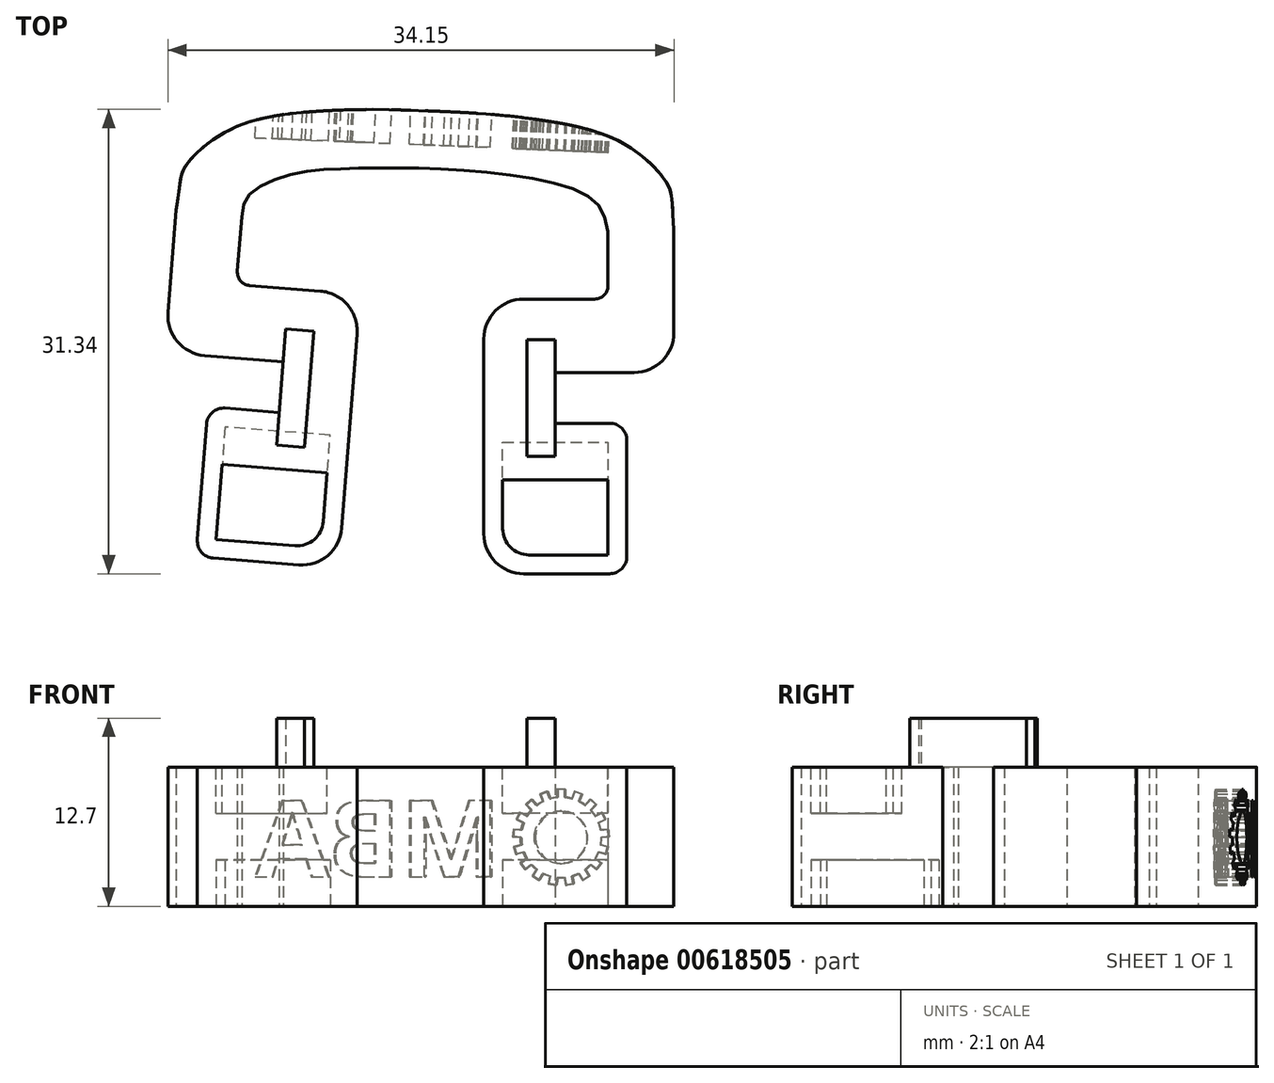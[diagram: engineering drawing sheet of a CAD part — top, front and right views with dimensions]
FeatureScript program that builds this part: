
annotation { "Feature Type Name" : "Feature", "Feature Type Description" : "" }
export const myFeature = defineFeature(function(context is Context, id is Id, definition is map)
    precondition{}
    {
        {
            var Q0;
            Q0=qCreatedBy(makeId("Top.planeOp"),FACE);
            var sketch = newSketch(context, id + "F0", { "sketchPlane" : qUnion([Q0])});
            skLineSegment(sketch, "E0", {"start": v(2.7, -18.54) * mm, "end": v(8.48, -18.54) * mm});
            skLineSegment(sketch, "E1", {"start": v(9.65, -17.37) * mm, "end": v(9.65, -9.55) * mm});
            skLineSegment(sketch, "E2", {"start": v(8.48, -8.38) * mm, "end": v(4.83, -8.38) * mm});
            skLineSegment(sketch, "E3", {"start": v(4.83, -8.38) * mm, "end": v(4.83, -4.95) * mm});
            skLineSegment(sketch, "E4", {"start": v(4.83, -4.95) * mm, "end": v(10.13, -4.95) * mm});
            skLineSegment(sketch, "E5", {"start": v(12.83, -2.26) * mm, "end": v(12.83, 4.7) * mm});
            skLineSegment(sketch, "E6", {"start": v(0, -15.85) * mm, "end": v(0, -2.7) * mm});
            skPoint(sketch, "E7.visualSharp", {"position": v(12.83, -4.95) * mm});
            skArc(sketch, "E7.filletArc", {"start": v(10.13, -4.95) * mm, "mid": v(12.04, -4.16) * mm, "end": v(12.83, -2.26) * mm});
            skPoint(sketch, "E8.visualSharp", {"position": v(9.65, -18.54) * mm});
            skArc(sketch, "E8.filletArc", {"start": v(8.48, -18.54) * mm, "mid": v(9.31, -18.2) * mm, "end": v(9.65, -17.37) * mm});
            skPoint(sketch, "E9.visualSharp", {"position": v(9.65, -8.38) * mm});
            skArc(sketch, "E9.filletArc", {"start": v(9.65, -9.55) * mm, "mid": v(9.31, -8.72) * mm, "end": v(8.48, -8.38) * mm});
            skPoint(sketch, "E10.visualSharp", {"position": v(0, -18.54) * mm});
            skArc(sketch, "E10.filletArc", {"start": v(0, -15.85) * mm, "mid": v(0.79, -17.75) * mm, "end": v(2.7, -18.54) * mm});
            skLineSegment(sketch, "E11", {"start": v(2.7, 0) * mm, "end": v(7.48, 0) * mm});
            skLineSegment(sketch, "E12", {"start": v(8.38, 0.9) * mm, "end": v(8.38, 4.57) * mm});
            skPoint(sketch, "E13.visualSharp", {"position": v(0, 0) * mm});
            skArc(sketch, "E13.filletArc", {"start": v(2.7, 0) * mm, "mid": v(0.79, -0.79) * mm, "end": v(0, -2.7) * mm});
            skPoint(sketch, "E14.visualSharp", {"position": v(8.38, 0) * mm});
            skArc(sketch, "E14.filletArc", {"start": v(7.48, 0) * mm, "mid": v(8.12, 0.26) * mm, "end": v(8.38, 0.9) * mm});
            skFitSpline(sketch, "E15", {"points": [v(12.83, 4.7) * mm, v(12.43, 7.7) * mm, v(9.35, 10.54) * mm, v(3.79, 12.1) * mm, v(-3.68, 12.7) * mm], "startDerivative": vector(-2.52, 27.94) * mm, "endDerivative": vector(-36.03, 1.35) * mm});
            skPoint(sketch, "E16.endSnap0", {"position": v(5.59, -18.54) * mm});
            skArc(sketch, "E17.MirrorCS", {"start": v(-18.72, -8.43) * mm, "mid": v(-18.32, -7.64) * mm, "end": v(-17.47, -7.36) * mm});
            skArc(sketch, "E18.MirrorCS", {"start": v(-18.26, -17.5) * mm, "mid": v(-19.06, -17.09) * mm, "end": v(-19.34, -16.24) * mm});
            skArc(sketch, "E19.MirrorCS", {"start": v(-15.81, 0.92) * mm, "mid": v(-16.42, 1.23) * mm, "end": v(-16.64, 1.88) * mm});
            skArc(sketch, "E20.MirrorCS", {"start": v(-18.84, -3.81) * mm, "mid": v(-20.68, -2.88) * mm, "end": v(-21.32, -0.92) * mm});
            skArc(sketch, "E21.MirrorCS", {"start": v(-9.6, -15.47) * mm, "mid": v(-10.53, -17.3) * mm, "end": v(-12.5, -17.95) * mm});
            skArc(sketch, "E22.MirrorCS", {"start": v(-11.04, 0.54) * mm, "mid": v(-9.2, -0.4) * mm, "end": v(-8.56, -2.36) * mm});
            skLineSegment(sketch, "E23.MirrorCS", {"start": v(-17.47, -7.36) * mm, "end": v(-13.82, -7.65) * mm});
            skLineSegment(sketch, "E24.MirrorCS", {"start": v(-13.82, -7.65) * mm, "end": v(-13.55, -4.23) * mm});
            skLineSegment(sketch, "E25.MirrorCS", {"start": v(-11.04, 0.54) * mm, "end": v(-15.81, 0.92) * mm});
            skLineSegment(sketch, "E26.MirrorCS", {"start": v(-13.55, -4.23) * mm, "end": v(-18.84, -3.81) * mm});
            skLineSegment(sketch, "E27.MirrorCS", {"start": v(-16.64, 1.88) * mm, "end": v(-16.35, 5.54) * mm});
            skLineSegment(sketch, "E28.MirrorCS", {"start": v(-12.5, -17.95) * mm, "end": v(-18.26, -17.5) * mm});
            skFitSpline(sketch, "E29.MirrorCS", {"points": [v(-20.77, 6.02) * mm, v(-20.13, 8.98) * mm, v(-16.85, 11.57) * mm, v(-11.18, 12.68) * mm, v(-3.68, 12.7) * mm], "startDerivative": vector(4.7, 27.65) * mm, "endDerivative": vector(36.02, -1.48) * mm});
            skLineSegment(sketch, "E30.MirrorCS", {"start": v(-9.6, -15.47) * mm, "end": v(-8.56, -2.36) * mm});
            skPoint(sketch, "E31.MirrorP", {"position": v(-21.53, -3.6) * mm});
            skPoint(sketch, "E32.MirrorP", {"position": v(-8.35, 0.33) * mm});
            skPoint(sketch, "E33.MirrorP", {"position": v(-16.7, 0.99) * mm});
            skLineSegment(sketch, "E34.MirrorCS", {"start": v(-19.34, -16.24) * mm, "end": v(-18.72, -8.43) * mm});
            skLineSegment(sketch, "E35.MirrorCS", {"start": v(-21.32, -0.92) * mm, "end": v(-20.77, 6.02) * mm});
            skPoint(sketch, "E36.MirrorP", {"position": v(-19.43, -17.4) * mm});
            skPoint(sketch, "E37.MirrorP", {"position": v(-9.8, -18.16) * mm});
            skPoint(sketch, "E38.MirrorP", {"position": v(-18.63, -7.27) * mm});
            skPoint(sketch, "E39.MirrorP", {"position": v(-15.38, -17.72) * mm});
            skFitSpline(sketch, "E40", {"points": [v(-16.35, 5.54) * mm, v(-15.64, 7.24) * mm, v(-12.74, 8.47) * mm, v(-9.06, 8.82) * mm, v(-3.88, 8.82) * mm, v(2.92, 8.2) * mm, v(7.36, 6.71) * mm, v(8.38, 4.57) * mm], "startDerivative": vector(0.51, 21.81) * mm, "endDerivative": vector(4.3, -24.8) * mm});
            skSolve(sketch);
        }
        {
            var Q0;
            Q0=makeQuery(id+"F0.imprint","IMPRINT",FACE,{"disambiguationData":[TD([[makeQuery(id+"F0.imprint","IMPRINT",EDGE,{"derivedFrom":sQuery(id+"F0.wireOp",EDGE,"E0")}),1.0]])]});
            extrude(context, id + "F1", {"entities" : qUnion([Q0]), "depth" : 9.4 * mm, "offsetDistance" : 25.4 * mm});
        }
        {
            var Q0;
            Q0=makeQuery(id+"F1.opExtrude","CAP_FACE",FACE,{"disambiguationData":[OSD([sQuery(id+"F0.wireOp",EDGE,"E0"),sQuery(id+"F0.wireOp",EDGE,"E1"),sQuery(id+"F0.wireOp",EDGE,"E2"),sQuery(id+"F0.wireOp",EDGE,"E3"),sQuery(id+"F0.wireOp",EDGE,"E4"),sQuery(id+"F0.wireOp",EDGE,"E5"),sQuery(id+"F0.wireOp",EDGE,"E6"),sQuery(id+"F0.wireOp",EDGE,"E7.filletArc"),sQuery(id+"F0.wireOp",EDGE,"E8.filletArc"),sQuery(id+"F0.wireOp",EDGE,"E9.filletArc"),sQuery(id+"F0.wireOp",EDGE,"E10.filletArc"),sQuery(id+"F0.wireOp",EDGE,"E11"),sQuery(id+"F0.wireOp",EDGE,"E12"),sQuery(id+"F0.wireOp",EDGE,"E13.filletArc"),sQuery(id+"F0.wireOp",EDGE,"E14.filletArc"),sQuery(id+"F0.wireOp",EDGE,"E15"),sQuery(id+"F0.wireOp",EDGE,"E17.MirrorCS"),sQuery(id+"F0.wireOp",EDGE,"E18.MirrorCS"),sQuery(id+"F0.wireOp",EDGE,"E19.MirrorCS"),sQuery(id+"F0.wireOp",EDGE,"E20.MirrorCS"),sQuery(id+"F0.wireOp",EDGE,"E21.MirrorCS"),sQuery(id+"F0.wireOp",EDGE,"E22.MirrorCS"),sQuery(id+"F0.wireOp",EDGE,"E23.MirrorCS"),sQuery(id+"F0.wireOp",EDGE,"E24.MirrorCS"),sQuery(id+"F0.wireOp",EDGE,"E25.MirrorCS"),sQuery(id+"F0.wireOp",EDGE,"E26.MirrorCS"),sQuery(id+"F0.wireOp",EDGE,"E27.MirrorCS"),sQuery(id+"F0.wireOp",EDGE,"E28.MirrorCS"),sQuery(id+"F0.wireOp",EDGE,"E29.MirrorCS"),sQuery(id+"F0.wireOp",EDGE,"E30.MirrorCS"),sQuery(id+"F0.wireOp",EDGE,"E34.MirrorCS"),sQuery(id+"F0.wireOp",EDGE,"E35.MirrorCS"),sQuery(id+"F0.wireOp",EDGE,"E40")])],"isStart":false});
            var sketch = newSketch(context, id + "F2", { "sketchPlane" : qUnion([Q0])});
            skPoint(sketch, "E41.endSnap0", {"position": v(-10.53, -17.3) * mm});
            skLineSegment(sketch, "E42", {"start": v(-10.72, -13.57) * mm, "end": v(-10.83, -15.02) * mm});
            skLineSegment(sketch, "E43", {"start": v(-18.06, -16.23) * mm, "end": v(-17.66, -11.17) * mm});
            skLineSegment(sketch, "E44", {"start": v(-18.06, -16.23) * mm, "end": v(-12.74, -16.65) * mm});
            skPoint(sketch, "E45.visualSharp", {"position": v(-10.97, -16.8) * mm});
            skArc(sketch, "E45.filletArc", {"start": v(-12.74, -16.65) * mm, "mid": v(-11.45, -16.23) * mm, "end": v(-10.83, -15.02) * mm});
            skLineSegment(sketch, "E46", {"start": v(-17.66, -11.17) * mm, "end": v(-10.57, -11.73) * mm});
            skLineSegment(sketch, "E47", {"start": v(-10.72, -13.57) * mm, "end": v(-10.57, -11.73) * mm});
            skPoint(sketch, "E48", {"position": v(-10.57, -11.73) * mm});
            skLineSegment(sketch, "E49.MirrorCS", {"start": v(1.27, -14.04) * mm, "end": v(1.27, -12.2) * mm});
            skPoint(sketch, "E50.MirrorP", {"position": v(1.27, -12.2) * mm});
            skPoint(sketch, "E51.MirrorP", {"position": v(0.79, -17.75) * mm});
            skLineSegment(sketch, "E52.MirrorCS", {"start": v(8.38, -17.27) * mm, "end": v(3.05, -17.27) * mm});
            skLineSegment(sketch, "E53.MirrorCS", {"start": v(8.38, -17.27) * mm, "end": v(8.38, -12.2) * mm});
            skLineSegment(sketch, "E54.MirrorCS", {"start": v(8.38, -12.2) * mm, "end": v(1.27, -12.2) * mm});
            skLineSegment(sketch, "E55.MirrorCS", {"start": v(1.27, -14.04) * mm, "end": v(1.27, -15.5) * mm});
            skArc(sketch, "E56.MirrorCS", {"start": v(3.05, -17.27) * mm, "mid": v(1.8, -16.75) * mm, "end": v(1.27, -15.5) * mm});
            skSolve(sketch);
        }
        {
            var Q0;
            Q0=makeQuery(id+"F2.imprint","IMPRINT",FACE,{"disambiguationData":[TD([[makeQuery(id+"F2.imprint","IMPRINT",EDGE,{"derivedFrom":sQuery(id+"F2.wireOp",EDGE,"E42")}),-1.0]])]});
            var Q1;
            Q1=makeQuery(id+"F2.imprint","IMPRINT",FACE,{"disambiguationData":[TD([[makeQuery(id+"F2.imprint","IMPRINT",EDGE,{"derivedFrom":sQuery(id+"F2.wireOp",EDGE,"E49.MirrorCS")}),-1.0]])]});
            extrude(context, id + "F3", {"entities" : qUnion([Q0, Q1]), "operationType" : NewBodyOperationType.REMOVE, "oppositeDirection" : true, "depth" : 3.12 * mm, "offsetDistance" : 25.4 * mm});
        }
        {
            var Q0;
            Q0=makeQuery(id+"F1.opExtrude","CAP_FACE",FACE,{"disambiguationData":[OSD([sQuery(id+"F0.wireOp",EDGE,"E0"),sQuery(id+"F0.wireOp",EDGE,"E1"),sQuery(id+"F0.wireOp",EDGE,"E2"),sQuery(id+"F0.wireOp",EDGE,"E3"),sQuery(id+"F0.wireOp",EDGE,"E4"),sQuery(id+"F0.wireOp",EDGE,"E5"),sQuery(id+"F0.wireOp",EDGE,"E6"),sQuery(id+"F0.wireOp",EDGE,"E7.filletArc"),sQuery(id+"F0.wireOp",EDGE,"E8.filletArc"),sQuery(id+"F0.wireOp",EDGE,"E9.filletArc"),sQuery(id+"F0.wireOp",EDGE,"E10.filletArc"),sQuery(id+"F0.wireOp",EDGE,"E11"),sQuery(id+"F0.wireOp",EDGE,"E12"),sQuery(id+"F0.wireOp",EDGE,"E13.filletArc"),sQuery(id+"F0.wireOp",EDGE,"E14.filletArc"),sQuery(id+"F0.wireOp",EDGE,"E15"),sQuery(id+"F0.wireOp",EDGE,"E17.MirrorCS"),sQuery(id+"F0.wireOp",EDGE,"E18.MirrorCS"),sQuery(id+"F0.wireOp",EDGE,"E19.MirrorCS"),sQuery(id+"F0.wireOp",EDGE,"E20.MirrorCS"),sQuery(id+"F0.wireOp",EDGE,"E21.MirrorCS"),sQuery(id+"F0.wireOp",EDGE,"E22.MirrorCS"),sQuery(id+"F0.wireOp",EDGE,"E23.MirrorCS"),sQuery(id+"F0.wireOp",EDGE,"E24.MirrorCS"),sQuery(id+"F0.wireOp",EDGE,"E25.MirrorCS"),sQuery(id+"F0.wireOp",EDGE,"E26.MirrorCS"),sQuery(id+"F0.wireOp",EDGE,"E27.MirrorCS"),sQuery(id+"F0.wireOp",EDGE,"E28.MirrorCS"),sQuery(id+"F0.wireOp",EDGE,"E29.MirrorCS"),sQuery(id+"F0.wireOp",EDGE,"E30.MirrorCS"),sQuery(id+"F0.wireOp",EDGE,"E34.MirrorCS"),sQuery(id+"F0.wireOp",EDGE,"E35.MirrorCS"),sQuery(id+"F0.wireOp",EDGE,"E40")])],"isStart":true});
            var sketch = newSketch(context, id + "F4", { "sketchPlane" : qUnion([Q0])});
            skLineSegment(sketch, "E57", {"start": v(8.38, 17.27) * mm, "end": v(3.05, 17.27) * mm});
            skLineSegment(sketch, "E58", {"start": v(1.27, 15.5) * mm, "end": v(1.27, 9.65) * mm});
            skLineSegment(sketch, "E59", {"start": v(1.27, 9.65) * mm, "end": v(8.38, 9.65) * mm});
            skLineSegment(sketch, "E60", {"start": v(8.38, 9.65) * mm, "end": v(8.38, 17.27) * mm});
            skPoint(sketch, "E61.visualSharp", {"position": v(1.27, 17.27) * mm});
            skArc(sketch, "E61.filletArc", {"start": v(3.05, 17.27) * mm, "mid": v(1.8, 16.75) * mm, "end": v(1.27, 15.5) * mm});
            skLineSegment(sketch, "E62.MirrorCS", {"start": v(-18.06, 16.23) * mm, "end": v(-12.74, 16.65) * mm});
            skPoint(sketch, "E63.MirrorP", {"position": v(-10.97, 16.8) * mm});
            skLineSegment(sketch, "E64.MirrorCS", {"start": v(-10.37, 9.2) * mm, "end": v(-17.46, 8.64) * mm});
            skLineSegment(sketch, "E65.MirrorCS", {"start": v(-17.46, 8.64) * mm, "end": v(-18.06, 16.23) * mm});
            skLineSegment(sketch, "E66.MirrorCS", {"start": v(-10.83, 15.02) * mm, "end": v(-10.37, 9.2) * mm});
            skArc(sketch, "E67.MirrorCS", {"start": v(-12.74, 16.65) * mm, "mid": v(-11.45, 16.23) * mm, "end": v(-10.83, 15.02) * mm});
            skSolve(sketch);
        }
        {
            var Q0;
            Q0 = qSketchRegion(id + "F4", true);
            extrude(context, id + "F5", {"entities" : qUnion([Q0]), "operationType" : NewBodyOperationType.REMOVE, "oppositeDirection" : true, "depth" : 3.12 * mm, "offsetDistance" : 25.4 * mm});
        }
        {
            var Q0;
            Q0=makeQuery(id+"F1.opExtrude","CAP_FACE",FACE,{"disambiguationData":[OSD([sQuery(id+"F0.wireOp",EDGE,"E0"),sQuery(id+"F0.wireOp",EDGE,"E1"),sQuery(id+"F0.wireOp",EDGE,"E2"),sQuery(id+"F0.wireOp",EDGE,"E3"),sQuery(id+"F0.wireOp",EDGE,"E4"),sQuery(id+"F0.wireOp",EDGE,"E5"),sQuery(id+"F0.wireOp",EDGE,"E6"),sQuery(id+"F0.wireOp",EDGE,"E7.filletArc"),sQuery(id+"F0.wireOp",EDGE,"E8.filletArc"),sQuery(id+"F0.wireOp",EDGE,"E9.filletArc"),sQuery(id+"F0.wireOp",EDGE,"E10.filletArc"),sQuery(id+"F0.wireOp",EDGE,"E11"),sQuery(id+"F0.wireOp",EDGE,"E12"),sQuery(id+"F0.wireOp",EDGE,"E13.filletArc"),sQuery(id+"F0.wireOp",EDGE,"E14.filletArc"),sQuery(id+"F0.wireOp",EDGE,"E15"),sQuery(id+"F0.wireOp",EDGE,"E17.MirrorCS"),sQuery(id+"F0.wireOp",EDGE,"E18.MirrorCS"),sQuery(id+"F0.wireOp",EDGE,"E19.MirrorCS"),sQuery(id+"F0.wireOp",EDGE,"E20.MirrorCS"),sQuery(id+"F0.wireOp",EDGE,"E21.MirrorCS"),sQuery(id+"F0.wireOp",EDGE,"E22.MirrorCS"),sQuery(id+"F0.wireOp",EDGE,"E23.MirrorCS"),sQuery(id+"F0.wireOp",EDGE,"E24.MirrorCS"),sQuery(id+"F0.wireOp",EDGE,"E25.MirrorCS"),sQuery(id+"F0.wireOp",EDGE,"E26.MirrorCS"),sQuery(id+"F0.wireOp",EDGE,"E27.MirrorCS"),sQuery(id+"F0.wireOp",EDGE,"E28.MirrorCS"),sQuery(id+"F0.wireOp",EDGE,"E29.MirrorCS"),sQuery(id+"F0.wireOp",EDGE,"E30.MirrorCS"),sQuery(id+"F0.wireOp",EDGE,"E34.MirrorCS"),sQuery(id+"F0.wireOp",EDGE,"E35.MirrorCS"),sQuery(id+"F0.wireOp",EDGE,"E40")])],"isStart":false});
            var sketch = newSketch(context, id + "F6", { "sketchPlane" : qUnion([Q0])});
            skLineSegment(sketch, "E68", {"start": v(-13.55, -4.23) * mm, "end": v(-13.38, -2.02) * mm});
            skLineSegment(sketch, "E69", {"start": v(-13.82, -7.65) * mm, "end": v(-14, -9.87) * mm});
            skLineSegment(sketch, "E70", {"start": v(-13.38, -2.02) * mm, "end": v(-11.48, -2.16) * mm});
            skLineSegment(sketch, "E71", {"start": v(-11.48, -2.16) * mm, "end": v(-12.1, -10.01) * mm});
            skLineSegment(sketch, "E72", {"start": v(-12.1, -10.01) * mm, "end": v(-14, -9.87) * mm});
            skLineSegment(sketch, "E73", {"start": v(4.83, -4.95) * mm, "end": v(4.83, -2.73) * mm});
            skLineSegment(sketch, "E74", {"start": v(4.83, -2.73) * mm, "end": v(2.92, -2.73) * mm});
            skLineSegment(sketch, "E75", {"start": v(2.92, -2.73) * mm, "end": v(2.92, -10.6) * mm});
            skLineSegment(sketch, "E76", {"start": v(2.92, -10.6) * mm, "end": v(4.83, -10.6) * mm});
            skLineSegment(sketch, "E77", {"start": v(4.83, -10.6) * mm, "end": v(4.83, -8.38) * mm});
            skSolve(sketch);
        }
        {
            var Q0;
            Q0=makeQuery(id+"F6.imprint","IMPRINT",FACE,{"disambiguationData":[TD([[makeQuery(id+"F6.imprint","IMPRINT",EDGE,{"derivedFrom":sQuery(id+"F6.wireOp",EDGE,"E68")}),-1.0]])]});
            var Q1;
            Q1=makeQuery(id+"F6.imprint","IMPRINT",FACE,{"disambiguationData":[TD([[makeQuery(id+"F6.imprint","IMPRINT",EDGE,{"derivedFrom":sQuery(id+"F6.wireOp",EDGE,"E73")}),1.0]])]});
            extrude(context, id + "F7", {"entities" : qUnion([Q0, Q1]), "operationType" : NewBodyOperationType.ADD, "depth" : 3.3 * mm, "offsetDistance" : 25.4 * mm});
        }
        {
            var Q0;
            Q0=makeQuery(id+"F1.opExtrude","CAP_FACE",FACE,{"disambiguationData":[OSD([sQuery(id+"F0.wireOp",EDGE,"E0"),sQuery(id+"F0.wireOp",EDGE,"E1"),sQuery(id+"F0.wireOp",EDGE,"E2"),sQuery(id+"F0.wireOp",EDGE,"E3"),sQuery(id+"F0.wireOp",EDGE,"E4"),sQuery(id+"F0.wireOp",EDGE,"E5"),sQuery(id+"F0.wireOp",EDGE,"E6"),sQuery(id+"F0.wireOp",EDGE,"E7.filletArc"),sQuery(id+"F0.wireOp",EDGE,"E8.filletArc"),sQuery(id+"F0.wireOp",EDGE,"E9.filletArc"),sQuery(id+"F0.wireOp",EDGE,"E10.filletArc"),sQuery(id+"F0.wireOp",EDGE,"E11"),sQuery(id+"F0.wireOp",EDGE,"E12"),sQuery(id+"F0.wireOp",EDGE,"E13.filletArc"),sQuery(id+"F0.wireOp",EDGE,"E14.filletArc"),sQuery(id+"F0.wireOp",EDGE,"E15"),sQuery(id+"F0.wireOp",EDGE,"E17.MirrorCS"),sQuery(id+"F0.wireOp",EDGE,"E18.MirrorCS"),sQuery(id+"F0.wireOp",EDGE,"E19.MirrorCS"),sQuery(id+"F0.wireOp",EDGE,"E20.MirrorCS"),sQuery(id+"F0.wireOp",EDGE,"E21.MirrorCS"),sQuery(id+"F0.wireOp",EDGE,"E22.MirrorCS"),sQuery(id+"F0.wireOp",EDGE,"E23.MirrorCS"),sQuery(id+"F0.wireOp",EDGE,"E24.MirrorCS"),sQuery(id+"F0.wireOp",EDGE,"E25.MirrorCS"),sQuery(id+"F0.wireOp",EDGE,"E26.MirrorCS"),sQuery(id+"F0.wireOp",EDGE,"E27.MirrorCS"),sQuery(id+"F0.wireOp",EDGE,"E28.MirrorCS"),sQuery(id+"F0.wireOp",EDGE,"E29.MirrorCS"),sQuery(id+"F0.wireOp",EDGE,"E30.MirrorCS"),sQuery(id+"F0.wireOp",EDGE,"E34.MirrorCS"),sQuery(id+"F0.wireOp",EDGE,"E35.MirrorCS"),sQuery(id+"F0.wireOp",EDGE,"E40")])],"isStart":false});
            var sketch = newSketch(context, id + "F8", { "sketchPlane" : qUnion([Q0])});
            skLineSegment(sketch, "E78", {"start": v(-3.68, 12.7) * mm, "end": v(-3.56, 15.72) * mm, "construction": true});
            skLineSegment(sketch, "E79", {"start": v(-5.82, 15.82) * mm, "end": v(-1.3, 15.63) * mm, "construction": true});
            skSolve(sketch);
        }
        {
            var Q0;
            Q0=sQuery(id+"F8.wireOp",EDGE,"E78");
            cPlane(context, id + "F9", {"entities" : qUnion([Q0]), "cplaneType" : CPlaneType.MID_PLANE, "offset" : 25.4 * mm, "width" : 152.4 * mm, "height" : 152.4 * mm});
        }
        {
            var Q0;
            Q0=qCreatedBy(id+"F9.planeOp",FACE);
            var sketch = newSketch(context, id + "F10", { "sketchPlane" : qUnion([Q0])});
            skText(sketch, "E80", { "text": "MBA", "fontName": "OpenSans-Bold.ttf"});
            skArc(sketch, "E81", {"start": v(-5.98, 7.09) * mm, "mid": v(-6.2, 6.97) * mm, "end": v(-6.4, 6.83) * mm});
            skCircle(sketch, "E82", {"center": v(-4.76, 4.65) * mm, "radius": 1.77 * mm});
            skLineSegment(sketch, "E83", {"start": v(-5.02, 7.36) * mm, "end": v(-5.02, 7.88) * mm});
            skLineSegment(sketch, "E84", {"start": v(-5.02, 7.88) * mm, "end": v(-4.5, 7.88) * mm});
            skLineSegment(sketch, "E85", {"start": v(-4.5, 7.88) * mm, "end": v(-4.5, 7.36) * mm});
            skLineSegment(sketch, "E86.1.0", {"start": v(-6.17, 7.57) * mm, "end": v(-5.68, 7.76) * mm});
            skLineSegment(sketch, "E86.1.1", {"start": v(-5.68, 7.76) * mm, "end": v(-5.5, 7.27) * mm});
            skLineSegment(sketch, "E86.1.2", {"start": v(-5.98, 7.09) * mm, "end": v(-6.17, 7.57) * mm});
            skLineSegment(sketch, "E86.2.0", {"start": v(-7.13, 6.86) * mm, "end": v(-6.74, 7.21) * mm});
            skLineSegment(sketch, "E86.2.1", {"start": v(-6.74, 7.21) * mm, "end": v(-6.4, 6.83) * mm});
            skLineSegment(sketch, "E86.2.2", {"start": v(-6.78, 6.48) * mm, "end": v(-7.13, 6.86) * mm});
            skLineSegment(sketch, "E87.1.3.0", {"start": v(-7.77, 5.86) * mm, "end": v(-7.53, 6.32) * mm});
            skLineSegment(sketch, "E87.3.3.0", {"start": v(-7.53, 6.32) * mm, "end": v(-7.07, 6.1) * mm});
            skLineSegment(sketch, "E87.6.3.0", {"start": v(-7.3, 5.63) * mm, "end": v(-7.77, 5.86) * mm});
            skLineSegment(sketch, "E87.1.4.0", {"start": v(-8, 4.7) * mm, "end": v(-7.95, 5.2) * mm});
            skLineSegment(sketch, "E87.3.4.0", {"start": v(-7.95, 5.2) * mm, "end": v(-7.44, 5.16) * mm});
            skLineSegment(sketch, "E87.6.4.0", {"start": v(-7.48, 4.64) * mm, "end": v(-8, 4.7) * mm});
            skLineSegment(sketch, "E87.1.5.0", {"start": v(-7.8, 3.52) * mm, "end": v(-7.94, 4.02) * mm});
            skLineSegment(sketch, "E87.3.5.0", {"start": v(-7.94, 4.02) * mm, "end": v(-7.44, 4.16) * mm});
            skLineSegment(sketch, "E87.6.5.0", {"start": v(-7.3, 3.66) * mm, "end": v(-7.8, 3.52) * mm});
            skLineSegment(sketch, "E87.1.6.0", {"start": v(-7.18, 2.5) * mm, "end": v(-7.5, 2.91) * mm});
            skLineSegment(sketch, "E87.3.6.0", {"start": v(-7.5, 2.91) * mm, "end": v(-7.08, 3.22) * mm});
            skLineSegment(sketch, "E87.6.6.0", {"start": v(-6.77, 2.81) * mm, "end": v(-7.18, 2.5) * mm});
            skLineSegment(sketch, "E87.1.7.0", {"start": v(-6.24, 1.77) * mm, "end": v(-6.68, 2.04) * mm});
            skLineSegment(sketch, "E87.3.7.0", {"start": v(-6.68, 2.04) * mm, "end": v(-6.4, 2.48) * mm});
            skLineSegment(sketch, "E87.6.7.0", {"start": v(-5.97, 2.2) * mm, "end": v(-6.24, 1.77) * mm});
            skLineSegment(sketch, "E87.1.8.0", {"start": v(-5.1, 1.43) * mm, "end": v(-5.6, 1.52) * mm});
            skLineSegment(sketch, "E87.3.8.0", {"start": v(-5.6, 1.52) * mm, "end": v(-5.51, 2.03) * mm});
            skLineSegment(sketch, "E87.6.8.0", {"start": v(-5, 1.94) * mm, "end": v(-5.1, 1.43) * mm});
            skLineSegment(sketch, "E87.1.9.0", {"start": v(-3.91, 1.52) * mm, "end": v(-4.42, 1.43) * mm});
            skLineSegment(sketch, "E87.3.9.0", {"start": v(-4.42, 1.43) * mm, "end": v(-4.52, 1.94) * mm});
            skLineSegment(sketch, "E87.6.9.0", {"start": v(-4, 2.03) * mm, "end": v(-3.91, 1.52) * mm});
            skLineSegment(sketch, "E87.1.10.0", {"start": v(-2.84, 2.04) * mm, "end": v(-3.28, 1.77) * mm});
            skLineSegment(sketch, "E87.3.10.0", {"start": v(-3.28, 1.77) * mm, "end": v(-3.55, 2.2) * mm});
            skLineSegment(sketch, "E87.6.10.0", {"start": v(-3.11, 2.48) * mm, "end": v(-2.84, 2.04) * mm});
            skLineSegment(sketch, "E87.1.11.0", {"start": v(-2.03, 2.91) * mm, "end": v(-2.34, 2.5) * mm});
            skLineSegment(sketch, "E87.3.11.0", {"start": v(-2.34, 2.5) * mm, "end": v(-2.75, 2.81) * mm});
            skLineSegment(sketch, "E87.6.11.0", {"start": v(-2.44, 3.22) * mm, "end": v(-2.03, 2.91) * mm});
            skLineSegment(sketch, "E87.1.12.0", {"start": v(-1.58, 4.02) * mm, "end": v(-1.72, 3.52) * mm});
            skLineSegment(sketch, "E87.3.12.0", {"start": v(-1.72, 3.52) * mm, "end": v(-2.22, 3.66) * mm});
            skLineSegment(sketch, "E87.6.12.0", {"start": v(-2.08, 4.16) * mm, "end": v(-1.58, 4.02) * mm});
            skLineSegment(sketch, "E87.1.13.0", {"start": v(-1.57, 5.2) * mm, "end": v(-1.52, 4.7) * mm});
            skLineSegment(sketch, "E87.3.13.0", {"start": v(-1.52, 4.7) * mm, "end": v(-2.03, 4.64) * mm});
            skLineSegment(sketch, "E87.6.13.0", {"start": v(-2.08, 5.16) * mm, "end": v(-1.57, 5.2) * mm});
            skLineSegment(sketch, "E87.1.14.0", {"start": v(-1.98, 6.32) * mm, "end": v(-1.75, 5.86) * mm});
            skLineSegment(sketch, "E87.3.14.0", {"start": v(-1.75, 5.86) * mm, "end": v(-2.22, 5.63) * mm});
            skLineSegment(sketch, "E87.6.14.0", {"start": v(-2.45, 6.1) * mm, "end": v(-1.98, 6.32) * mm});
            skLineSegment(sketch, "E87.1.15.0", {"start": v(-2.77, 7.21) * mm, "end": v(-2.4, 6.86) * mm});
            skLineSegment(sketch, "E87.3.15.0", {"start": v(-2.4, 6.86) * mm, "end": v(-2.74, 6.48) * mm});
            skLineSegment(sketch, "E87.6.15.0", {"start": v(-3.12, 6.83) * mm, "end": v(-2.77, 7.21) * mm});
            skLineSegment(sketch, "E87.1.16.0", {"start": v(-3.83, 7.76) * mm, "end": v(-3.35, 7.57) * mm});
            skLineSegment(sketch, "E87.3.16.0", {"start": v(-3.35, 7.57) * mm, "end": v(-3.54, 7.09) * mm});
            skLineSegment(sketch, "E87.6.16.0", {"start": v(-4.02, 7.27) * mm, "end": v(-3.83, 7.76) * mm});
            skArc(sketch, "E88.trimOffspring", {"start": v(-5.02, 7.36) * mm, "mid": v(-5.26, 7.33) * mm, "end": v(-5.5, 7.27) * mm});
            skArc(sketch, "E89.trimOffspring", {"start": v(-4.02, 7.27) * mm, "mid": v(-4.26, 7.33) * mm, "end": v(-4.5, 7.36) * mm});
            skArc(sketch, "E90.trimOffspring", {"start": v(-3.12, 6.83) * mm, "mid": v(-3.32, 6.97) * mm, "end": v(-3.54, 7.09) * mm});
            skArc(sketch, "E91.trimOffspring", {"start": v(-2.45, 6.1) * mm, "mid": v(-2.58, 6.3) * mm, "end": v(-2.74, 6.48) * mm});
            skArc(sketch, "E92.trimOffspring", {"start": v(-2.08, 5.16) * mm, "mid": v(-2.14, 5.4) * mm, "end": v(-2.22, 5.63) * mm});
            skArc(sketch, "E93.trimOffspring", {"start": v(-2.08, 4.16) * mm, "mid": v(-2.05, 4.4) * mm, "end": v(-2.03, 4.64) * mm});
            skArc(sketch, "E94.trimOffspring", {"start": v(-2.44, 3.22) * mm, "mid": v(-2.32, 3.44) * mm, "end": v(-2.22, 3.66) * mm});
            skArc(sketch, "E95.trimOffspring", {"start": v(-3.11, 2.48) * mm, "mid": v(-2.92, 2.64) * mm, "end": v(-2.75, 2.81) * mm});
            skArc(sketch, "E96.trimOffspring", {"start": v(-4, 2.03) * mm, "mid": v(-3.77, 2.11) * mm, "end": v(-3.55, 2.2) * mm});
            skArc(sketch, "E97.trimOffspring", {"start": v(-5, 1.94) * mm, "mid": v(-4.76, 1.93) * mm, "end": v(-4.52, 1.94) * mm});
            skArc(sketch, "E98.trimOffspring", {"start": v(-5.97, 2.2) * mm, "mid": v(-5.74, 2.11) * mm, "end": v(-5.51, 2.03) * mm});
            skArc(sketch, "E99.trimOffspring", {"start": v(-6.77, 2.81) * mm, "mid": v(-6.6, 2.64) * mm, "end": v(-6.4, 2.48) * mm});
            skArc(sketch, "E100.trimOffspring", {"start": v(-7.3, 3.66) * mm, "mid": v(-7.2, 3.44) * mm, "end": v(-7.08, 3.22) * mm});
            skArc(sketch, "E101.trimOffspring", {"start": v(-7.48, 4.64) * mm, "mid": v(-7.47, 4.4) * mm, "end": v(-7.44, 4.16) * mm});
            skArc(sketch, "E102.trimOffspring", {"start": v(-7.3, 5.63) * mm, "mid": v(-7.38, 5.4) * mm, "end": v(-7.44, 5.16) * mm});
            skArc(sketch, "E103.trimOffspring", {"start": v(-6.78, 6.48) * mm, "mid": v(-6.93, 6.3) * mm, "end": v(-7.07, 6.1) * mm});
            const initialGuessF10  = {"E80": [-0.00067, 0.002, 1, 0, 0.00517]};
            skSetInitialGuess(sketch, initialGuessF10);
            skSolve(sketch);
        }
        {
            var Q0;
            Q0 = qSketchRegion(id + "F10", true);
            extrude(context, id + "F11", {"entities" : qUnion([Q0]), "operationType" : NewBodyOperationType.REMOVE, "oppositeDirection" : true, "depth" : 3.8 * mm, "offsetDistance" : 25.4 * mm});
        }
    });
